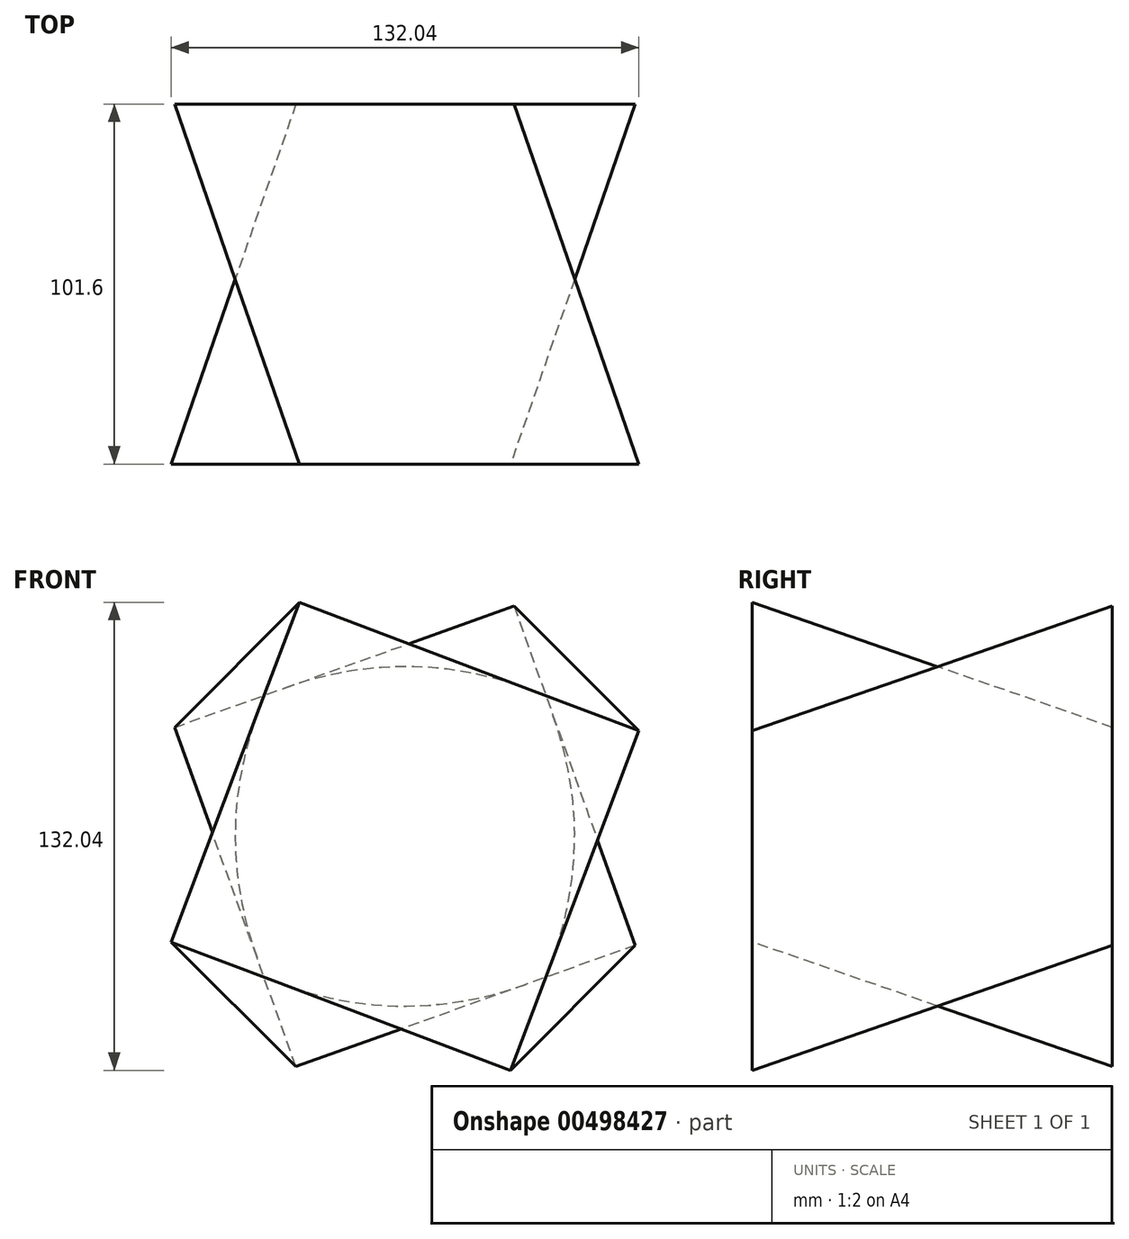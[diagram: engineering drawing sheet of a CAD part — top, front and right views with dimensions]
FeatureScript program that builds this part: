
annotation { "Feature Type Name" : "Feature", "Feature Type Description" : "" }
export const myFeature = defineFeature(function(context is Context, id is Id, definition is map)
    precondition{}
    {
        {
            var Q0;
            Q0=qCreatedBy(makeId("Front.planeOp"),FACE);
            var sketch = newSketch(context, id + "F0", { "sketchPlane" : qUnion([Q0])});
            skCircle(sketch, "E0.cCircle", {"center": v(0, 0) * mm, "radius": 71.88 * mm, "construction": true});
            skLineSegment(sketch, "E0.0", {"start": v(30.75, 64.97) * mm, "end": v(64.97, -30.75) * mm});
            skLineSegment(sketch, "E0.1", {"start": v(64.97, -30.75) * mm, "end": v(-30.75, -64.97) * mm});
            skLineSegment(sketch, "E0.2", {"start": v(-30.75, -64.97) * mm, "end": v(-64.97, 30.75) * mm});
            skLineSegment(sketch, "E0.3", {"start": v(-64.97, 30.75) * mm, "end": v(30.75, 64.97) * mm});
            skSolve(sketch);
        }
        {
            var Q0;
            Q0=qCreatedBy(makeId("Front.planeOp"),FACE);
            cPlane(context, id + "F1", {"entities" : qUnion([Q0]), "cplaneType" : CPlaneType.OFFSET, "offset" : 101.6 * mm, "width" : 152.4 * mm, "height" : 152.4 * mm});
        }
        {
            var Q0;
            Q0=qCreatedBy(id+"F1.planeOp",FACE);
            var sketch = newSketch(context, id + "F2", { "sketchPlane" : qUnion([Q0])});
            skCircle(sketch, "E1.cCircle", {"center": v(0, 0) * mm, "radius": 72.44 * mm, "construction": true});
            skLineSegment(sketch, "E1.0", {"start": v(-29.81, 66.02) * mm, "end": v(66.02, 29.81) * mm});
            skLineSegment(sketch, "E1.1", {"start": v(66.02, 29.81) * mm, "end": v(29.81, -66.02) * mm});
            skLineSegment(sketch, "E1.2", {"start": v(29.81, -66.02) * mm, "end": v(-66.02, -29.81) * mm});
            skLineSegment(sketch, "E1.3", {"start": v(-66.02, -29.81) * mm, "end": v(-29.81, 66.02) * mm});
            skSolve(sketch);
        }
        {
            var Q0;
            Q0=makeQuery(id+"F0.imprint","IMPRINT",FACE,{"disambiguationData":[TD([[makeQuery(id+"F0.imprint","IMPRINT",EDGE,{"derivedFrom":sQuery(id+"F0.wireOp",EDGE,"E0.0")}),-1.0]])]});
            var Q1;
            Q1=makeQuery(id+"F2.imprint","IMPRINT",FACE,{"disambiguationData":[TD([[makeQuery(id+"F2.imprint","IMPRINT",EDGE,{"derivedFrom":sQuery(id+"F2.wireOp",EDGE,"E1.0")}),-1.0]])]});
            loft(context, id + "F3", {"sheetProfilesArray" : [{ "sheetProfileEntities" : qUnion([Q0]) }, { "sheetProfileEntities" : qUnion([Q1]) }]});
        }
    });
